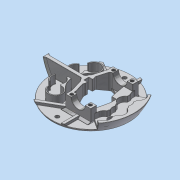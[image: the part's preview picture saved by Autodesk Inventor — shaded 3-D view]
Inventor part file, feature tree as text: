
AUTODESK INVENTOR PART (.ipt)
format: ipt  version: 2017 (Build 210142000, 142)  size: 2,477,568 bytes
history: native  units: mm
features: fillet x36, projected_geometry x31, sketch x29, extrude x20, plane x8, hole x7, mirror x4, revolve x3, other x3, loft x2, chamfer x2, pattern_circular x1
ambient origin geometry x8: Origin, YZ Plane, XZ Plane, XY Plane, X Axis, Y Axis, Z Axis, Center Point
bodies: Volumenkörper1 (feature_tree)
feature tree (146):
  revolve  "Umdrehung1"
  sketch  "Skizze6"  dims[d7=5.0mm d8=90.0deg]
  plane  "Arbeitsebene2"
  sketch  "Skizze7"  dims[d28=0.25mm d36=4.0mm]
  plane  "Arbeitsebene3"
  sketch  "Skizze8"  dims[d38=2.0mm d40=1.2mm]
  loft  "Erhebung1"
  extrude  "Extrusion16"  TaperAngle=90.0deg  [1 undecoded]
  other  "Rippe1"
  extrude  "Extrusion17"  Depth=4.0mm
  extrude  "Extrusion21"  Depth=1.2mm
  hole  "Bohrung4"  [1 undecoded]
  hole  "Bohrung3"  [1 undecoded]
  plane  "Arbeitsebene11"
  mirror  "Spiegeln6"
  mirror  "Spiegeln3"
  extrude  "Extrusion18"  TaperAngle=0.0deg  [1 undecoded]
  extrude  "Extrusion20"  TaperAngle=60.0deg  [1 undecoded]
  sketch  "Skizze37"  dims[d63=2.5mm d64=1.0mm d65=0.0mm d66=0.0mm d67=1.0mm d68=1.0mm d82=51.0mm]
  extrude  "Extrusion19"  Depth=51.0mm
  extrude  "Extrusion22"  Depth=53.0mm
  plane  "Arbeitsebene13"
  extrude  "Extrusion23"  Depth=1.0mm
  extrude  "Extrusion24"  Depth=8.0mm
  chamfer  "Fase3"  Distance=10.0mm
  chamfer  "Fase2"  Distance=10.0mm
  mirror  "Spiegeln8"
  plane  "Arbeitsebene14"
  plane  "Arbeitsebene1"
  hole  "Bohrung1"  [1 undecoded]
  fillet  "Rundung2"  Radius=17.348736mm
  extrude  "Extrusion29"  TaperAngle=90.0deg  [1 undecoded]
  extrude  "Extrusion28"  Depth=5.25mm
  extrude  "Extrusion31"  Depth=3.490659mm
  loft  "Erhebung3"
  sketch  "Skizze57"  dims[d184=2.459mm d185=6.0mm d186=4.0mm d187=2.0mm d188=90.0deg d189=8.8mm d190=20.594885mm d191=6.0mm d194=17.348736mm]
  plane  "Arbeitsebene16"
  extrude  "Extrusion32"  Depth=7.0mm TaperAngle=0.0deg
  sketch  "Skizze61"  dims[d206=90.0deg d207=5.25mm]
  extrude  "Extrusion34"  TaperAngle=90.0deg  [1 undecoded]
  hole  "Bohrung5"  [1 undecoded]
  pattern_circular  "Runde Anordnung1"  [2 undecoded]
  revolve  "Umdrehung9"
  revolve  "Umdrehung10"
  extrude  "Extrusion35"  Depth=0.2mm
  extrude  "Extrusion36"  Depth=0.2mm
  fillet  "Rundung5"  Radius=15.0mm
  extrude  "Extrusion37"  Depth=0.2mm
  extrude  "Extrusion38"  Depth=0.2mm
  fillet  "Rundung6"  Radius=5.0mm
  fillet  "Rundung8"  Radius=15.0mm
  fillet  "Rundung9"  Radius=2.0mm
  fillet  "Rundung10"  Radius=1.0mm
  fillet  "Rundung11"  Radius=1.5mm
  fillet  "Rundung12"  Radius=9.699mm
  fillet  "Rundung13"  [1 undecoded]
  fillet  "Rundung14"  Radius=1.0mm
  fillet  "Rundung15"  Radius=0.8mm
  fillet  "Rundung17"  Radius=10.0mm
  fillet  "Rundung18"  Radius=6.0mm
  fillet  "Rundung19"  Radius=37.5mm
  fillet  "Rundung20"  Radius=13.919411mm
  fillet  "Rundung21"  Radius=8.905149mm
  fillet  "Rundung22"  Radius=27.925268mm
  fillet  "Rundung24"  Radius=37.5mm
  fillet  "Rundung25"  Radius=8.905149mm
  fillet  "Rundung26"  [1 undecoded]
  fillet  "Rundung27"  Radius=17.0mm
  fillet  "Rundung28"  Radius=10.0mm
  fillet  "Rundung29"  Radius=22.0mm
  fillet  "Rundung30"  Radius=5.0mm
  fillet  "Rundung31"  Radius=17.0mm
  fillet  "Rundung32"  [1 undecoded]
  fillet  "Rundung34"  [1 undecoded]
  fillet  "Rundung35"  Radius=10.5mm
  fillet  "Rundung36"  [1 undecoded]
  fillet  "Rundung39"  Radius=8.0mm
  hole  "Bohrung6"  [1 undecoded]
  hole  "Bohrung7"  [1 undecoded]
  hole  "Bohrung8"  [1 undecoded]
  fillet  "Rundung40"  Radius=4.5mm
  extrude  "Extrusion39"  Depth=0.2mm
  fillet  "Rundung41"  Radius=5.0mm
  fillet  "Rundung42"  [1 undecoded]
  fillet  "Rundung43"  Radius=5.5mm
  fillet  "Rundung44"  [1 undecoded]
  sketch  "Skizze74"  dims[d244=5.0mm d245=2.0mm d246=4.0mm d247=3.0mm d248=15.0mm d249=0.0mm d252=3.0mm d253=1.0mm d255=5.0mm d257=15.0mm d258=0.0mm d259=2.0mm d262=11.0mm d263=5.0mm d264=45.0deg d266=1.0mm d268=1.5mm d269=9.699mm d270=5.0mm d271=45.0deg d272=0.0mm d276=1.0mm d277=0.8mm d292=10.0mm d293=6.0mm d294=37.5mm d295=13.919411mm d296=8.905149mm d297=27.925268mm d298=37.5mm d302=8.905149mm d303=0.0mm d304=17.0mm d305=10.0mm d306=0.0mm d310=22.0mm d311=5.0mm d312=0.0mm d313=17.0mm d314=0.0mm d315=90.0deg d316=0.0mm d317=90.0deg d318=10.5mm d325=0.0mm d326=8.0mm d327=4.363323mm d328=3.2mm d329=4.5mm d330=4.5mm d331=3.2mm d332=5.0mm d333=0.0mm d334=5.5mm d335=120.0deg d336=2.38157mm d339=2.5mm d340=0.0mm d341=3.2mm d342=6.0mm d343=4.0mm d344=2.0mm d345=90.0deg d346=8.0mm d347=20.594885mm d348=60.0mm d349=360.0deg d351=90.0deg d352=2.0mm d353=90.0deg d354=10.5mm d355=10.5mm d356=10.5mm d357=10.5mm d358=4.5mm d359=0.0mm d361=8.0mm d362=7.0mm d363=10.0mm d364=0.0mm d372=1.0mm d373=10.0mm d374=0.0mm d375=10.0mm d376=0.0mm d381=7.0mm d382=0.2mm d384=0.2mm d385=0.2mm d386=0.2mm d387=0.2mm d388=0.2mm d389=0.2mm d390=0.2mm d391=0.2mm d393=0.2mm d394=0.2mm d395=0.2mm d396=0.2mm d397=0.2mm d398=7.0mm d399=0.2mm d401=0.2mm d402=0.2mm d403=0.2mm d404=0.2mm d405=0.2mm d406=0.2mm d407=0.2mm d408=0.2mm d409=0.2mm d411=0.2mm d412=0.2mm d413=0.2mm d416=0.1mm d417=29.0mm d418=29.0mm d419=3.0mm d420=6.0mm d421=4.0mm d422=2.0mm d423=90.0deg d424=8.0mm d425=20.594885mm d426=3.0mm d427=6.0mm d428=4.0mm d429=2.0mm d430=90.0deg d431=8.0mm d432=20.594885mm d439=3.0mm d440=6.0mm d441=4.0mm d442=2.0mm d443=90.0deg d444=8.0mm d445=20.594885mm d449=0.2mm d455=5.7mm d456=3.5mm d457=0.0mm d458=0.2mm d459=0.2mm d460=0.2mm d461=0.2mm d464=9.5mm d465=2.0mm d467=0.2mm d468=2.5mm d469=10.0mm d470=0.0mm]
  plane  "Arbeitsebene17"
  extrude  "Extrusion41"  Depth=0.2mm
  mirror  "Spiegeln11"
  fillet  "Rundung45"  Radius=2.5mm
  sketch  "Skizze1"  dims[d3=5.0mm d5=50.0mm]
  projected_geometry  "Projizierte Kontur1"
  sketch  "Skizze9"  dims[d41=45.0mm d49=4.0mm]
  projected_geometry  "Projizierte Kontur3"
  projected_geometry  "Projizierte Kontur4"
  projected_geometry  "Projizierte Kontur5"
  projected_geometry  "Projizierte Kontur6"
  sketch  "Skizze13"  dims[d50=22.0mm d51=5.0mm]
  projected_geometry  "Projizierte Kontur10"
  sketch  "Skizze31"  dims[d53=10.0mm d54=0.0mm d55=90.0deg]
  sketch  "Skizze32"  dims[d56=0.0mm d57=90.0deg d62=60.0deg]
  projected_geometry  "Projizierte Kontur20"
  projected_geometry  "Projizierte Kontur22"
  projected_geometry  "Projizierte Kontur23"
  sketch  "Skizze39"  dims[d83=45.0mm d84=53.0mm]
  projected_geometry  "Projizierte Kontur24"
  projected_geometry  "Projizierte Kontur25"
  projected_geometry  "Projizierte Kontur28"
  projected_geometry  "Projizierte Kontur29"
  sketch  "Skizze44"  dims[d85=60.0mm d87=360.0deg]
  projected_geometry  "Projizierte Kontur31"
  sketch  "Skizze46"  dims[d89=2.459mm d90=6.0mm d91=4.0mm d92=2.0mm d93=90.0deg d94=5.0mm d95=20.594885mm d97=1.0mm d98=25.0mm]
  projected_geometry  "Projizierte Kontur41"
  projected_geometry  "Projizierte Kontur42"
  projected_geometry  "Projizierte Kontur43"
  projected_geometry  "Projizierte Kontur49"
  sketch  "Skizze53"  dims[d99=8.0mm d130=8.0mm d176=10.0mm d177=0.0mm]
  sketch  "Skizze54"  dims[d179=3.0mm]
  sketch  "Skizze55"  dims[d180=25.0mm]
  sketch  "Skizze56"  dims[d181=12.0mm d182=10.0mm d183=0.0mm]
  projected_geometry  "Projizierte Kontur50"
  projected_geometry  "Projizierte Kontur51"
  sketch  "Skizze60"  dims[d201=9.0mm d202=0.0mm d203=90.0deg]
  sketch  "Skizze62"  dims[d208=90.0deg d209=3.490659mm]
  sketch  "Skizze64"  dims[d210=90.0deg d211=10.5mm]
  sketch  "Skizze65"  dims[d214=1.0mm d215=7.0mm d216=0.0mm]
  projected_geometry  "Projizierte Kontur54"
  sketch  "Skizze66"  dims[d218=120.0deg d220=90.0deg]
  sketch  "Skizze67"  dims[d222=10.0mm d223=0.0mm d224=60.0deg]
  projected_geometry  "Projizierte Kontur55"
  sketch  "Skizze68"  dims[d225=5.0mm]
  sketch  "Skizze69"  dims[d227=7.0mm d228=0.0mm]
  projected_geometry  "Projizierte Kontur56"
  projected_geometry  "Projizierte Kontur57"
  sketch  "Skizze70"  dims[d235=2.4mm d236=6.0mm d237=3.0mm d238=2.0mm d239=90.0deg d240=5.0mm d241=20.594885mm]
  projected_geometry  "Projizierte Kontur58"
  projected_geometry  "Projizierte Kontur59"
  sketch  "Skizze73"  dims[d242=7.0mm d243=0.0mm]
  projected_geometry  "Projizierte Kontur60"
  projected_geometry  "Projizierte Kontur61"
  projected_geometry  "Projizierte Kontur62"
  projected_geometry  "Projizierte Kontur63"
  projected_geometry  "Projizierte Kontur64"
  other  "Schnittkanten projizieren1"
  other  "Schnittkanten projizieren2"
note: 21 required parameter values undecoded (feature->parameter linkage not recoverable at this tier; creation-order binding heuristic only, values carry confidence <= 0.55)
